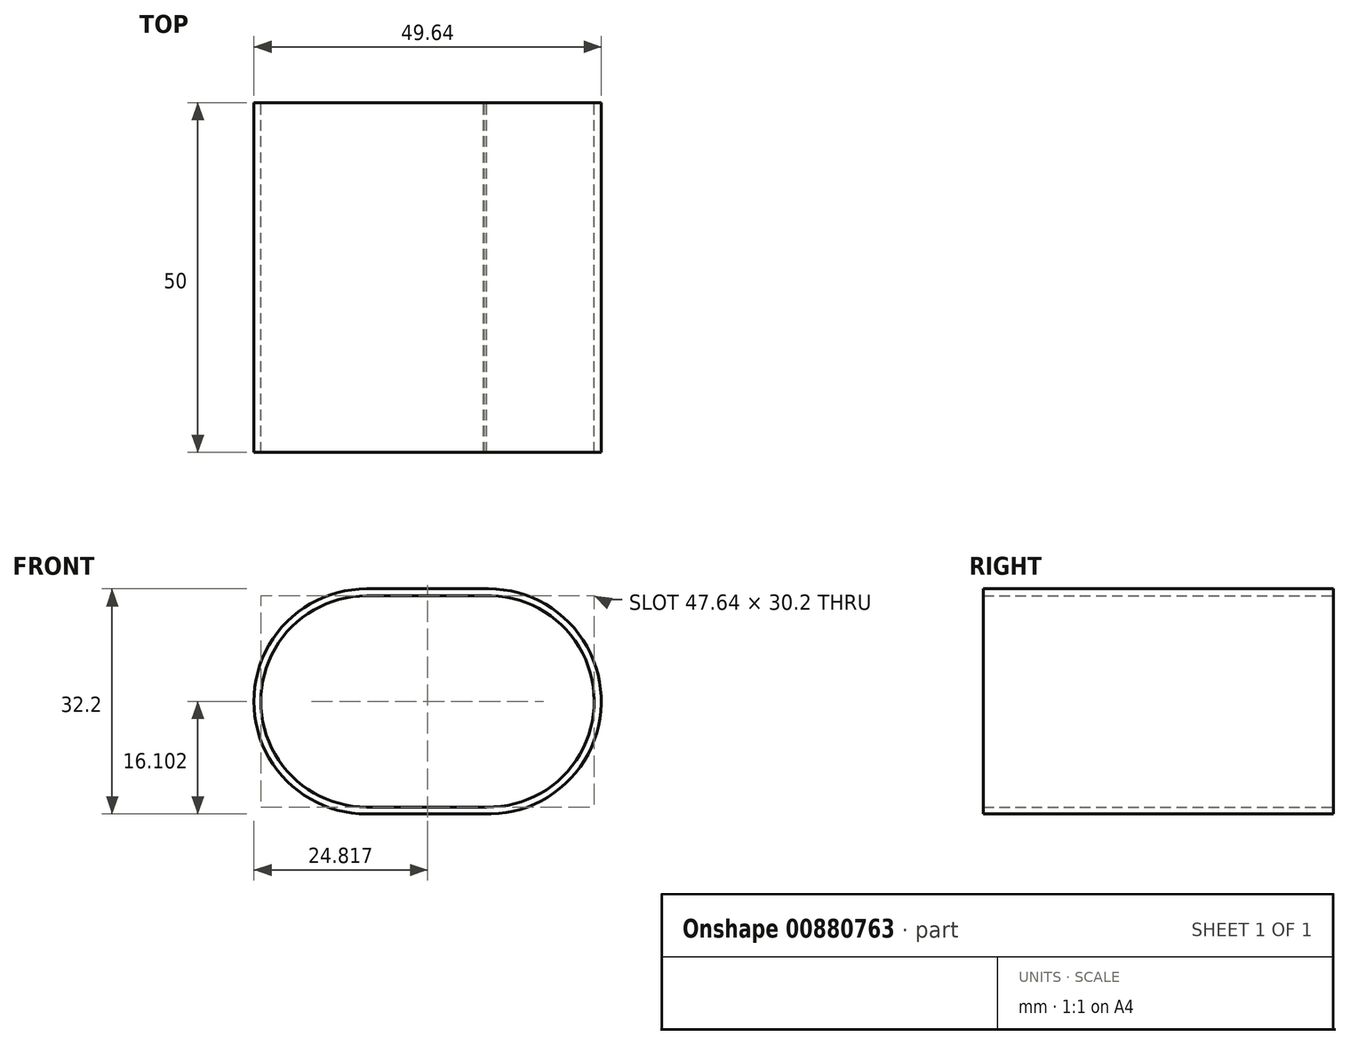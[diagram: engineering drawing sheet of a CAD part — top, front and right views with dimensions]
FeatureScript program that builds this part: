
annotation { "Feature Type Name" : "Feature", "Feature Type Description" : "" }
export const myFeature = defineFeature(function(context is Context, id is Id, definition is map)
    precondition{}
    {
        {
            var Q0;
            Q0=qCreatedBy(makeId("Front.planeOp"),FACE);
            var sketch = newSketch(context, id + "F0", { "sketchPlane" : qUnion([Q0])});
            skArc(sketch, "E0", {"start": v(0, 16.1) * mm, "mid": v(-16.1, 0) * mm, "end": v(0.02, -16.1) * mm});
            skArc(sketch, "E1", {"start": v(16.72, -16.08) * mm, "mid": v(33.53, -0.36) * mm, "end": v(17.44, 16.1) * mm});
            skLineSegment(sketch, "E2", {"start": v(0, 16.1) * mm, "end": v(17.44, 16.1) * mm});
            skLineSegment(sketch, "E3", {"start": v(0.02, -16.1) * mm, "end": v(18.18, -16.08) * mm});
            skSolve(sketch);
        }
        {
            var Q0;
            Q0 = qSketchRegion(id + "F0", true);
            extrude(context, id + "F1", {"entities" : qUnion([Q0]), "depth" : 40 * mm, "offsetDistance" : 25 * mm, "hasSecondDirection" : true, "secondDirectionOppositeDirection" : true, "secondDirectionDepth" : 10 * mm});
        }
        {
            var Q0;
            Q0=makeQuery(id+"F1.opExtrude","CAP_FACE",FACE,{"disambiguationData":[OSD([sQuery(id+"F0.wireOp",EDGE,"E0"),sQuery(id+"F0.wireOp",EDGE,"E1"),sQuery(id+"F0.wireOp",EDGE,"E2"),sQuery(id+"F0.wireOp",EDGE,"E3")])],"isStart":true});
            var sketch = newSketch(context, id + "F2", { "sketchPlane" : qUnion([Q0])});
            skArc(sketch, "E4", {"start": v(-16.83, 15.09) * mm, "mid": v(-32.53, 0.16) * mm, "end": v(-17.14, -15.1) * mm});
            skArc(sketch, "E5", {"start": v(0, -15.1) * mm, "mid": v(15.1, 0) * mm, "end": v(-0.01, 15.1) * mm});
            skLineSegment(sketch, "E6", {"start": v(-16.83, 15.09) * mm, "end": v(0, 15.1) * mm});
            skLineSegment(sketch, "E7", {"start": v(-17.73, -15.1) * mm, "end": v(0, -15.1) * mm});
            skSolve(sketch);
        }
        {
            var Q0;
            Q0 = qSketchRegion(id + "F2", true);
            extrude(context, id + "F3", {"entities" : qUnion([Q0]), "operationType" : NewBodyOperationType.REMOVE, "endBound" : BoundingType.THROUGH_ALL, "oppositeDirection" : true, "depth" : 25 * mm, "offsetDistance" : 25 * mm});
        }
    });
